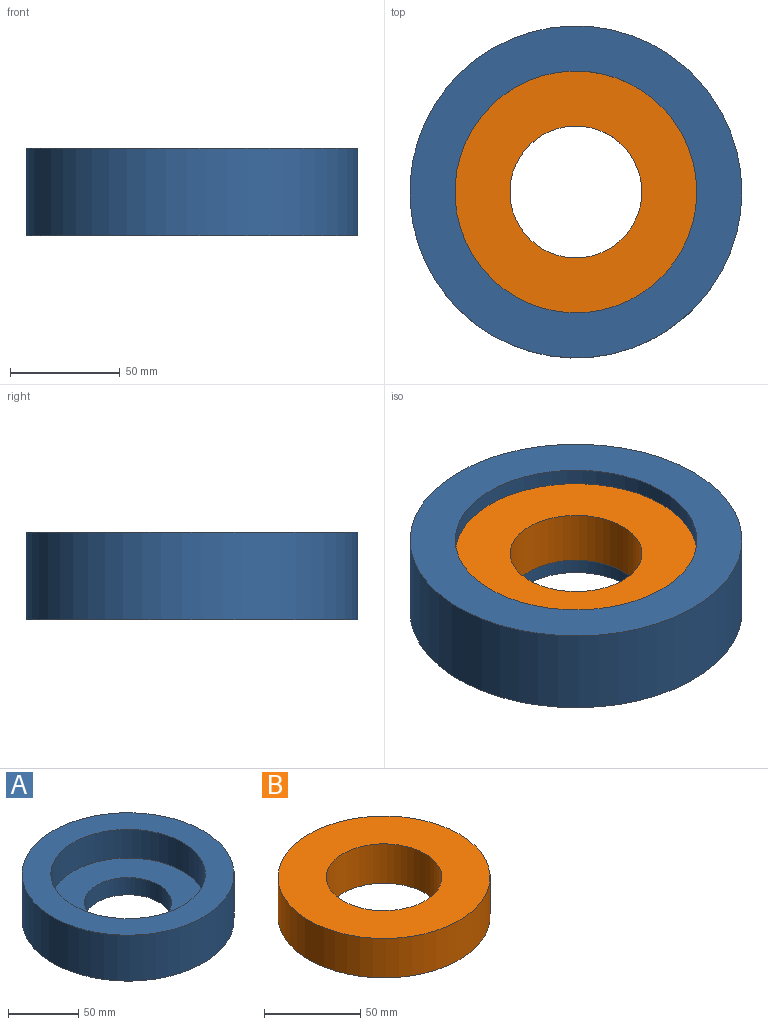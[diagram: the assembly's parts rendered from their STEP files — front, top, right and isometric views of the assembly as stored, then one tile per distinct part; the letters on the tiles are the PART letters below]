
ASSEMBLY  parts=2 mates=1
PART A: 6 faces, bbox 151x151x40 mm
  f0: cylinder r=55mm len=110mm, axis (0,0,-1), area 8639.4mm2, adj f2,f5
  f1: cylinder r=75.5mm len=151mm, axis (0,0,-1), area 18975.2mm2, adj f2,f3
  f2: plane 151x151mm, normal (0,0,1), area 8404.5mm2, adj f0,f1
  f3: plane 151x151mm, normal (0,0,-1), area 14888.8mm2, adj f1,f4
  f4: cylinder r=31mm len=62mm, axis (0,0,-1), area 2921.7mm2, adj f3,f5
  f5: plane 110x110mm, normal (0,0,1), area 6484.2mm2, adj f0,f4
PART B: 4 faces, bbox 110x110x25 mm
  f0: cylinder r=30mm len=60mm, axis (0,0,-1), area 4712.4mm2, adj f2,f3
  f1: cylinder r=55mm len=110mm, axis (0,0,-1), area 8639.4mm2, adj f2,f3
  f2: plane 110x110mm, normal (0,0,1), area 6675.9mm2, adj f0,f1
  f3: plane 110x110mm, normal (0,0,-1), area 6675.9mm2, adj f0,f1
PLACE A at identity
PLACE B t=(0,0,7.5)mm
MATE fastened B.f1 <-> A.f4  axis (0,0,-1) through (0,0,7.5)mm
